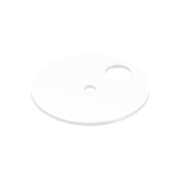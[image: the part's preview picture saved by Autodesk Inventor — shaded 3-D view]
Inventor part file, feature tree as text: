
AUTODESK INVENTOR PART (.ipt)
format: ipt  version: 2012 (Build 160160000, 160)  size: 80,384 bytes
history: native  units: mm
features: extrude x1, sketch x1
ambient origin geometry x8: Origin, YZ Plane, XZ Plane, XY Plane, X Axis, Y Axis, Z Axis, Center Point
feature tree (2):
  extrude  "Extrusion2"  Depth=9.18mm
  sketch  "Sketch1"  dims[d0=90.0mm d1=9.18mm d4=20.0mm d6=30.0mm d7=3.0mm d8=0.0mm]
